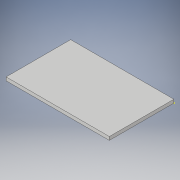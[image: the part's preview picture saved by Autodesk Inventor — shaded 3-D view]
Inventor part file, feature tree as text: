
AUTODESK INVENTOR PART (.ipt)
format: ipt  version: 2018 (Build 220112000, 112)  size: 89,600 bytes
history: native  units: in
note: dims shown in document units (in); Inventor stores cm internally (conversion verified against a paired STEP export)
features: sketch x2, extrude x1
ambient origin geometry x8: Origin, YZ Plane, XZ Plane, XY Plane, X Axis, Y Axis, Z Axis, Center Point
bodies: Solid1 (feature_tree)
feature tree (3):
  sketch  "Sketch1"  dims[d0=4.7835in d1=2.9921in]
  extrude  "Extrusion1"  Depth=2.9921in
  sketch  "Sketch2"  dims[d2=0.1555in d3=0.0in]
